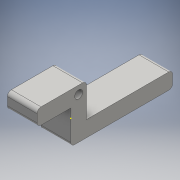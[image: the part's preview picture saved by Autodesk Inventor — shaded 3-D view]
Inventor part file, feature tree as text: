
AUTODESK INVENTOR PART (.ipt)
format: ipt  version: 2016 (Build 200138000, 138)  size: 135,680 bytes
history: native  units: mm
features: sketch x5, extrude x3, fillet x2, hole x1
ambient origin geometry x8: Origin, YZ Plane, XZ Plane, XY Plane, X Axis, Y Axis, Z Axis, Center Point
bodies: Solid1 (feature_tree)
feature tree (11):
  extrude  "Extrusion1"  Depth=25.0mm
  hole  "Hole1"  [1 undecoded]
  sketch  "Sketch4"  dims[d6=4.0mm]
  extrude  "Extrusion3"  Depth=8.0mm
  fillet  "Fillet3"  Radius=17.0mm
  extrude  "Extrusion4"  Depth=2.0mm
  fillet  "Fillet4"  Radius=8.0mm
  sketch  "Sketch1"  dims[d0=15.0mm d1=25.0mm]
  sketch  "Sketch2"  dims[d2=8.0mm d3=0.0mm d5=4.0mm]
  sketch  "Sketch5"  dims[d7=4.0mm d8=6.0mm d9=4.0mm d10=2.0mm d11=90.0deg d12=8.0mm d13=20.594885mm d20=8.0mm d21=17.0mm]
  sketch  "Sketch6"  dims[d22=15.0mm d23=0.0mm d24=2.0mm d25=8.0mm d26=43.5mm d27=15.0mm d28=0.0mm d29=2.0mm]
note: 1 required parameter value undecoded (feature->parameter linkage not recoverable at this tier; creation-order binding heuristic only, values carry confidence <= 0.55)
